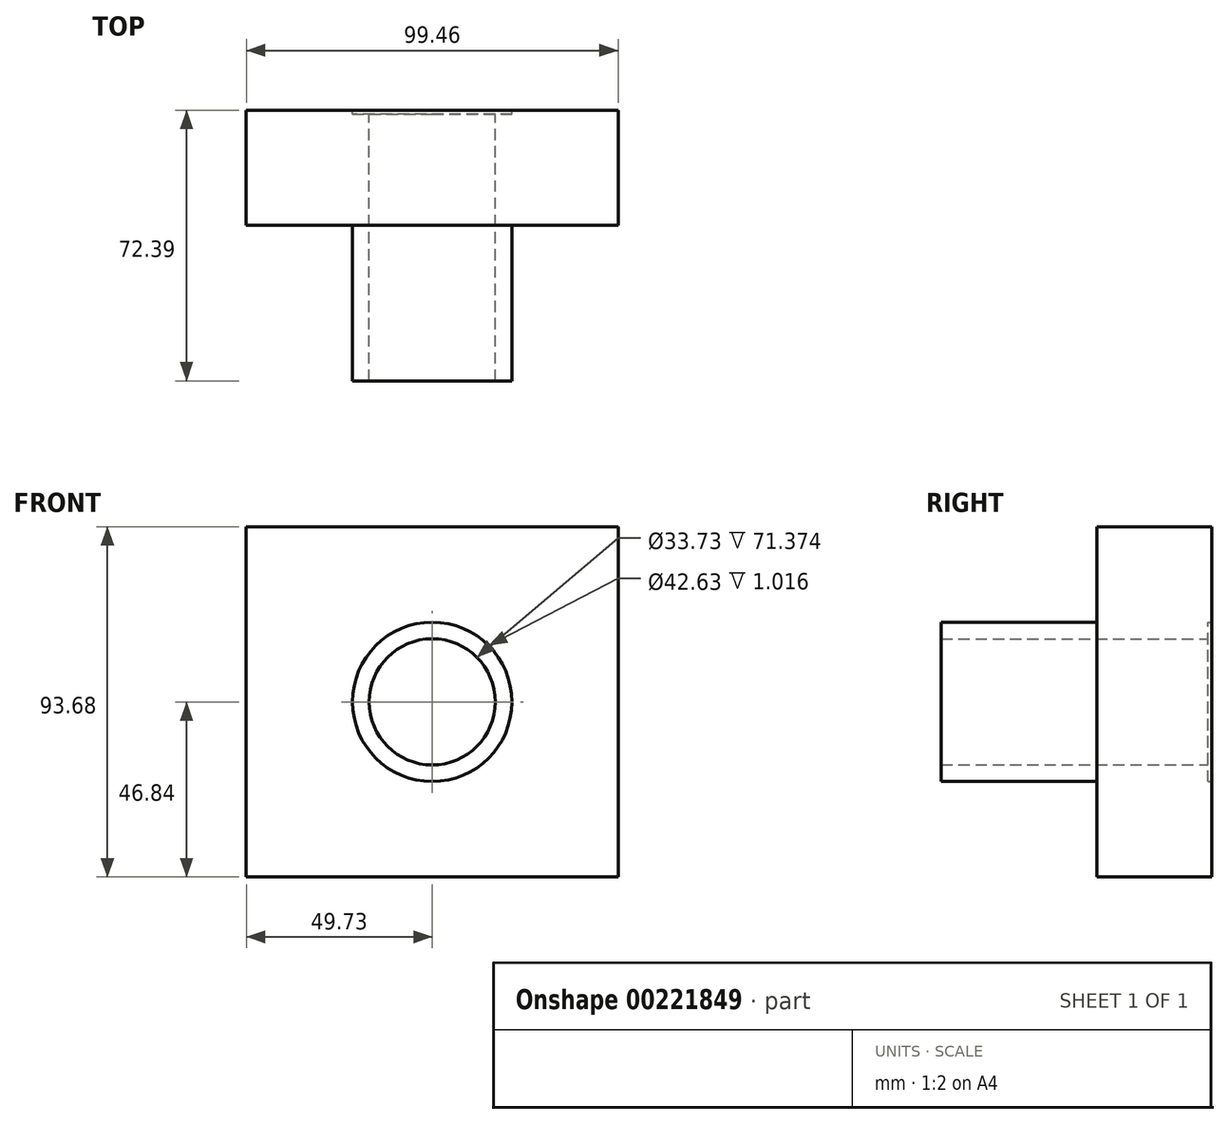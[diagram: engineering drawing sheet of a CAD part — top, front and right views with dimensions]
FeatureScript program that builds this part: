
annotation { "Feature Type Name" : "Feature", "Feature Type Description" : "" }
export const myFeature = defineFeature(function(context is Context, id is Id, definition is map)
    precondition{}
    {
        {
            var Q0;
            Q0=qCreatedBy(makeId("Front.planeOp"),FACE);
            var sketch = newSketch(context, id + "F0", { "sketchPlane" : qUnion([Q0])});
            skLineSegment(sketch, "E0.bottom", {"start": v(-49.73, 46.84) * mm, "end": v(49.73, 46.84) * mm});
            skLineSegment(sketch, "E0.top", {"start": v(-49.73, -46.84) * mm, "end": v(49.73, -46.84) * mm});
            skLineSegment(sketch, "E0.left", {"start": v(-49.73, 46.84) * mm, "end": v(-49.73, -46.84) * mm});
            skLineSegment(sketch, "E0.right", {"start": v(49.73, 46.84) * mm, "end": v(49.73, -46.84) * mm});
            skPoint(sketch, "E0.middle", {"position": v(0, 0) * mm});
            skSolve(sketch);
        }
        {
            var Q0;
            Q0=makeQuery(id+"F0.imprint","IMPRINT",FACE,{"disambiguationData":[TD([[makeQuery(id+"F0.imprint","IMPRINT",EDGE,{"derivedFrom":sQuery(id+"F0.wireOp",EDGE,"E0.bottom")}),-1.0]])]});
            extrude(context, id + "F1", {"entities" : qUnion([Q0]), "depth" : 30.73 * mm});
        }
        {
            var Q0;
            Q0=qCreatedBy(makeId("Front.planeOp"),FACE);
            var sketch = newSketch(context, id + "F2", { "sketchPlane" : qUnion([Q0])});
            skCircle(sketch, "E1", {"center": v(0, 0) * mm, "radius": 21.31 * mm});
            skCircle(sketch, "E2", {"center": v(0, 0) * mm, "radius": 16.87 * mm});
            skSolve(sketch);
        }
        {
            var Q0;
            Q0 = qSketchRegion(id + "F2", true);
            extrude(context, id + "F3", {"entities" : qUnion([Q0]), "operationType" : NewBodyOperationType.ADD, "depth" : 72.39 * mm});
        }
        {
            var Q0;
            Q0 = qSketchRegion(id + "F2", true);
            extrude(context, id + "F4", {"entities" : qUnion([Q0]), "operationType" : NewBodyOperationType.REMOVE, "depth" : 1.02 * mm});
        }
        {
            var Q0;
            Q0=qCreatedBy(makeId("Front.planeOp"),FACE);
            var sketch = newSketch(context, id + "F5", { "sketchPlane" : qUnion([Q0])});
            skSolve(sketch);
        }
        {
            var Q0;
            Q0 = qSketchRegion(id + "F5", true);
            var Q1;
            Q1=makeQuery(id+"F4.boolean.opBoolean","SPLIT",FACE,{"disambiguationData":[TD([makeQuery(id+"F4.opExtrude","SWEPT_FACE",FACE,{"disambiguationData":[OSD([sQuery(id+"F2.wireOp",EDGE,"E2")])]})])],"derivedFrom":makeQuery(id+"F1.opExtrude","CAP_FACE",FACE,{"disambiguationData":[OSD([sQuery(id+"F0.wireOp",EDGE,"E0.bottom"),sQuery(id+"F0.wireOp",EDGE,"E0.top"),sQuery(id+"F0.wireOp",EDGE,"E0.left"),sQuery(id+"F0.wireOp",EDGE,"E0.right")])],"isStart":true})});
            extrude(context, id + "F6", {"entities" : qUnion([Q0, Q1]), "operationType" : NewBodyOperationType.REMOVE, "oppositeDirection" : true, "depth" : 76.7 * mm});
        }
    });
